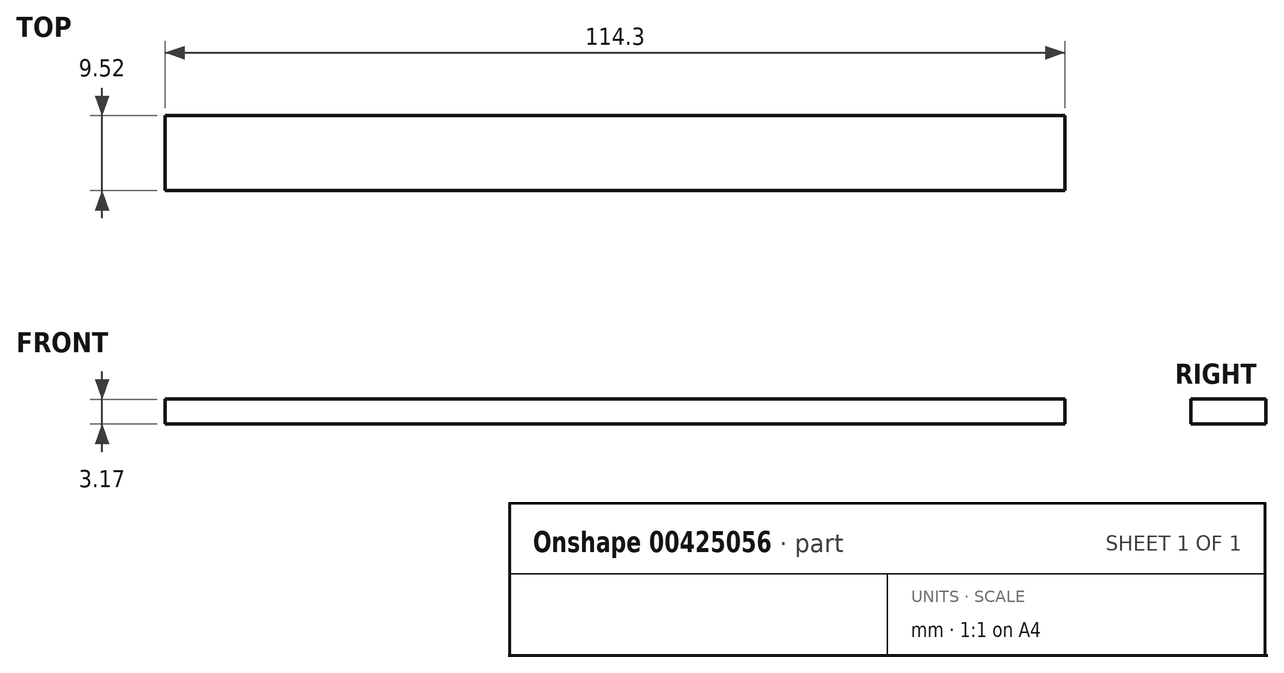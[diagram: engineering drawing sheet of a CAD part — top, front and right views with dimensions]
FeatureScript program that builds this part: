
annotation { "Feature Type Name" : "Feature", "Feature Type Description" : "" }
export const myFeature = defineFeature(function(context is Context, id is Id, definition is map)
    precondition{}
    {
        {
            var Q0;
            Q0=qCreatedBy(makeId("Top.planeOp"),FACE);
            var sketch = newSketch(context, id + "F0", { "sketchPlane" : qUnion([Q0])});
            skLineSegment(sketch, "E0.bottom", {"start": v(-61.28, 3.84) * mm, "end": v(53.02, 3.84) * mm});
            skLineSegment(sketch, "E0.top", {"start": v(-61.28, -5.68) * mm, "end": v(53.02, -5.68) * mm});
            skLineSegment(sketch, "E0.left", {"start": v(-61.28, 3.84) * mm, "end": v(-61.28, -5.68) * mm});
            skLineSegment(sketch, "E0.right", {"start": v(53.02, 3.84) * mm, "end": v(53.02, -5.68) * mm});
            skSolve(sketch);
        }
        {
            var Q0;
            Q0 = qSketchRegion(id + "F0", true);
            extrude(context, id + "F1", {"entities" : qUnion([Q0]), "depth" : 3.17 * mm});
        }
    });
